# Revit family: Shower-Bath_and_Shower_Trim-KOHLER-Stillness-K-T948
name_source: partatom
category: Plumbing Fixtures
revit_build: Autodesk Revit 2015 (Build: 20140606_1530(x64)
units: mm (PartAtom-declared; Revit-internal decimal feet)

## types (4) — shared parameters
ADA Compliant = No
Assembly Code = D2010700
CW Connection = No
Cold Water Inlet = Cold Water Inlet
Date Modified = 03/25/2019
Default Elevation = 42"
Drain Included = No
HW Connection = Yes
Height = 6 3/8"
Hot Water Inlet = Hot Water Inlet
Manufacturer = KOHLER Co.
MasterFormat 1995 = 15410
MasterFormat 2004 = 22.41.23
Material = Premium Material Construction
Product Documentation Link = https://www.us.kohler.com
Product Name = Stillness
Product Page URL = http://www.us.kohler.com
Tempered Water Inlet 1 = Tempered Water Inlet 1
Tempered Water Inlet 2 = Tempered Water Inlet 2
URL = https://www.us.kohler.com
Vent Connection = No
Waste Connection = No
Waste Water Outlet = Waste Water Outlet
WaterSense Certified = No
Width = 6 3/8"

## per-type parameters (varying)
| type | Description | Finish | Model | ShowerHead | Type | Without ShowerHead |
| With Shower CP-Polished Chrome | Rite-Temp pressure-balancing bath and shower faucet trim with lever handle, valve not included | Kohler-Metal-CP-Polished_Chrome | K-T948-4-CP | Yes | 1 | No |
| With Shower BN-Vibrant Brushed Nickel | Rite-Temp pressure-balancing bath and shower faucet trim with lever handle, valve not included | Kohler-Metal-BN-Vibrant_Brushed_Nickel | K-T948-4-BN | Yes | 2 | No |
| Without Shower CP-Polished Chrome | Rite-Temp bath and shower trim set with push-button diverter and lever handle, less showerhead | Kohler-Metal-CP-Polished_Chrome | K-T948-4L-CP | No | 3 | Yes |
| Without Shower BN-Vibrant Brushed Nickel | Rite-Temp bath and shower trim set with push-button diverter and lever handle, less showerhead | Kohler-Metal-BN-Vibrant_Brushed_Nickel | K-T948-4L-BN | No | 4 | Yes |

## geometry (parser evidence)
native form markers: Sweep x11
no freeform markers — native parametric forms only
